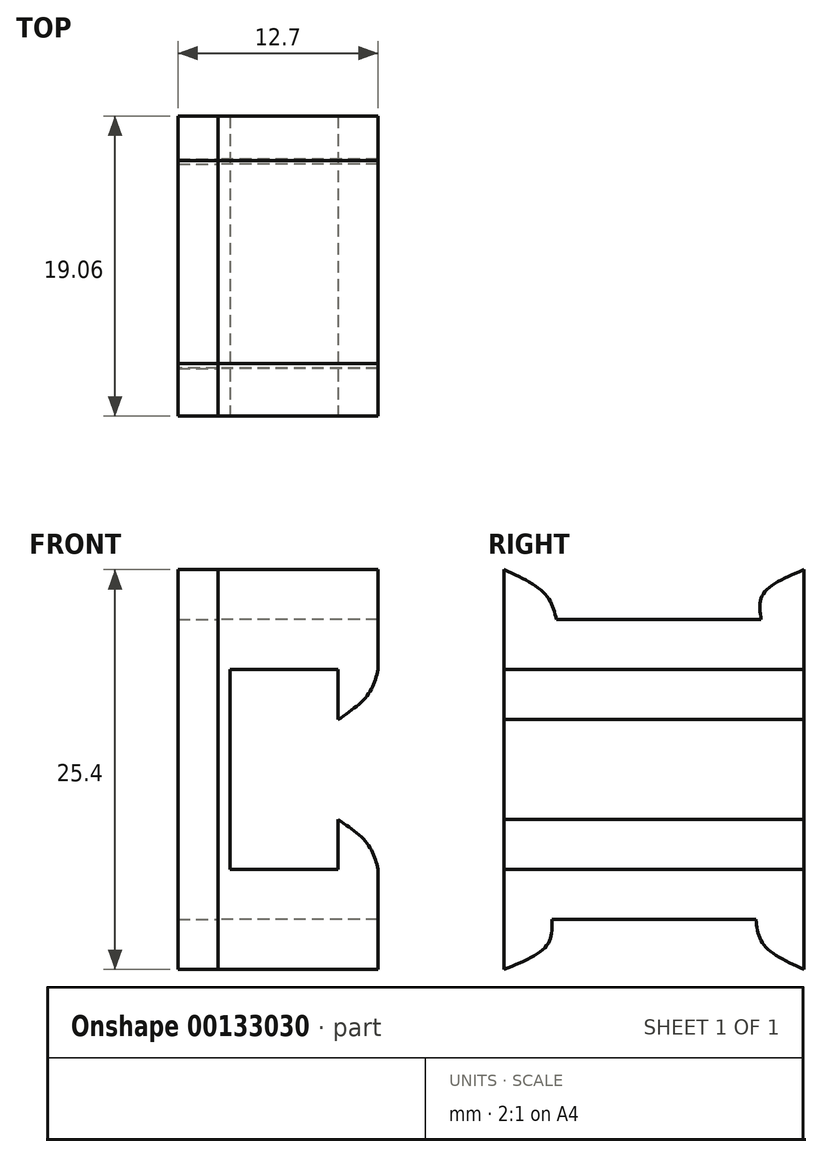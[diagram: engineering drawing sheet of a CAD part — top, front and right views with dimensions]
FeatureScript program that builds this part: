
annotation { "Feature Type Name" : "Feature", "Feature Type Description" : "" }
export const myFeature = defineFeature(function(context is Context, id is Id, definition is map)
    precondition{}
    {
        {
            var Q0;
            Q0=qCreatedBy(makeId("Right.planeOp"),FACE);
            var sketch = newSketch(context, id + "F0", { "sketchPlane" : qUnion([Q0])});
            skLineSegment(sketch, "E0.bottom", {"start": v(-9.53, 23.71) * mm, "end": v(9.52, 23.71) * mm});
            skLineSegment(sketch, "E0.top", {"start": v(-9.53, 42.76) * mm, "end": v(9.52, 42.76) * mm});
            skLineSegment(sketch, "E0.left", {"start": v(-9.53, 23.71) * mm, "end": v(-9.53, 42.76) * mm});
            skLineSegment(sketch, "E0.right", {"start": v(9.52, 23.71) * mm, "end": v(9.52, 42.76) * mm});
            skPoint(sketch, "E0.middle", {"position": v(0, 33.24) * mm});
            skLineSegment(sketch, "E1", {"start": v(9.52, 42.76) * mm, "end": v(9.52, 45.94) * mm});
            skLineSegment(sketch, "E2", {"start": v(-9.53, 42.76) * mm, "end": v(-9.53, 45.94) * mm});
            skLineSegment(sketch, "E3", {"start": v(-9.53, 23.71) * mm, "end": v(-9.53, 20.54) * mm});
            skLineSegment(sketch, "E4", {"start": v(9.52, 23.71) * mm, "end": v(9.52, 20.54) * mm});
            skPoint(sketch, "E5.1.internal.snap0", {"position": v(9.52, 22.13) * mm});
            skFitSpline(sketch, "E5", {"points": [v(9.53, 20.54) * mm, v(6.95, 22.13) * mm, v(6.47, 23.71) * mm], "startDerivative": vector(-5.44, 2.49) * mm, "endDerivative": vector(-0.42, 3.94) * mm});
            skFitSpline(sketch, "E6", {"points": [v(-9.52, 20.54) * mm, v(-6.77, 22.13) * mm, v(-6.5, 23.71) * mm], "startDerivative": vector(5.9, 2.4) * mm, "endDerivative": vector(-0.18, 4.04) * mm});
            skPoint(sketch, "E7.1.internal.snap0", {"position": v(-9.53, 44.35) * mm});
            skFitSpline(sketch, "E7", {"points": [v(-9.52, 45.94) * mm, v(-6.9, 44.35) * mm, v(-6.2, 42.76) * mm], "startDerivative": vector(5.47, -2.52) * mm, "endDerivative": vector(0.98, -3.9) * mm});
            skFitSpline(sketch, "E8", {"points": [v(9.53, 45.94) * mm, v(6.9, 44.35) * mm, v(6.8, 42.76) * mm], "startDerivative": vector(-5.76, -2.42) * mm, "endDerivative": vector(0.66, -4.01) * mm});
            skSolve(sketch);
        }
        {
            var Q0;
            {var subQ0=sQuery(id+"F0.wireOp",EDGE,"E0.left");Q0=makeQuery(id+"F0.imprint","IMPRINT",FACE,{"disambiguationData":[TD([[makeQuery(id+"F0.imprint","IMPRINT",EDGE,{"derivedFrom":subQ0}),-1.0]])]});}
            var Q1;
            {var subQ0=sQuery(id+"F0.wireOp",EDGE,"E2");Q1=makeQuery(id+"F0.imprint","IMPRINT",FACE,{"disambiguationData":[TD([[makeQuery(id+"F0.imprint","IMPRINT",EDGE,{"derivedFrom":subQ0}),-1.0]])]});}
            var Q2;
            {var subQ0=sQuery(id+"F0.wireOp",EDGE,"E1");Q2=makeQuery(id+"F0.imprint","IMPRINT",FACE,{"disambiguationData":[TD([[makeQuery(id+"F0.imprint","IMPRINT",EDGE,{"derivedFrom":subQ0}),1.0]])]});}
            var Q3;
            {var subQ0=sQuery(id+"F0.wireOp",EDGE,"E3");Q3=makeQuery(id+"F0.imprint","IMPRINT",FACE,{"disambiguationData":[TD([[makeQuery(id+"F0.imprint","IMPRINT",EDGE,{"derivedFrom":subQ0}),1.0]])]});}
            var Q4;
            {var subQ0=sQuery(id+"F0.wireOp",EDGE,"E4");Q4=makeQuery(id+"F0.imprint","IMPRINT",FACE,{"disambiguationData":[TD([[makeQuery(id+"F0.imprint","IMPRINT",EDGE,{"derivedFrom":subQ0}),-1.0]])]});}
            extrude(context, id + "F1", {"entities" : qUnion([Q0, Q1, Q2, Q3, Q4]), "endBound" : BoundingType.SYMMETRIC, "depth" : 10.16 * mm});
        }
        {
            var Q0;
            Q0=makeQuery(id+"F1.opExtrude","SWEPT_FACE",FACE,{"disambiguationData":[OSD([sQuery(id+"F0.wireOp",EDGE,"E0.left"),sQuery(id+"F0.wireOp",EDGE,"E2"),sQuery(id+"F0.wireOp",EDGE,"E3")])]});
            var sketch = newSketch(context, id + "F2", { "sketchPlane" : qUnion([Q0])});
            skPoint(sketch, "E9.endSnap0", {"position": v(0, 45.94) * mm});
            skLineSegment(sketch, "E10", {"start": v(-4.32, 39.59) * mm, "end": v(5.08, 39.59) * mm});
            skLineSegment(sketch, "E11", {"start": v(-4.32, 26.89) * mm, "end": v(5.08, 26.89) * mm});
            skLineSegment(sketch, "E12", {"start": v(-4.32, 39.59) * mm, "end": v(-4.32, 26.89) * mm});
            skSolve(sketch);
        }
        {
            var Q0;
            {var subQ0=sQuery(id+"F2.wireOp",EDGE,"E10");Q0=makeQuery(id+"F2.imprint","IMPRINT",FACE,{"disambiguationData":[TD([[makeQuery(id+"F2.imprint","IMPRINT",EDGE,{"derivedFrom":subQ0}),-1.0]])]});}
            extrude(context, id + "F3", {"entities" : qUnion([Q0]), "operationType" : NewBodyOperationType.REMOVE, "oppositeDirection" : true, "depth" : 36.4 * mm});
        }
        {
            var Q0;
            {var subQ0=sQuery(id+"F0.wireOp",EDGE,"E4");var subQ1=sQuery(id+"F0.wireOp",EDGE,"E1");var subQ2=sQuery(id+"F0.wireOp",EDGE,"E0.right");var subQ3=sQuery(id+"F0.wireOp",EDGE,"E3");var subQ4=sQuery(id+"F0.wireOp",EDGE,"E2");var subQ5=sQuery(id+"F0.wireOp",EDGE,"E0.left");var subQ6=sQuery(id+"F0.wireOp",EDGE,"E7");var subQ7=sQuery(id+"F0.wireOp",EDGE,"E0.top");var subQ8=sQuery(id+"F0.wireOp",EDGE,"E8");Q0=makeQuery(id+"F3.boolean.opBoolean","SPLIT",FACE,{"disambiguationData":[TD([makeQuery(id+"F1.opExtrude","SWEPT_FACE",FACE,{"disambiguationData":[OSD([subQ7])]})])],"derivedFrom":makeQuery(id+"F1.opExtrude","CAP_FACE",FACE,{"disambiguationData":[OSD([sQuery(id+"F0.wireOp",EDGE,"E0.bottom"),subQ7,subQ5,subQ2,subQ1,subQ4,subQ3,subQ0,sQuery(id+"F0.wireOp",EDGE,"E5"),sQuery(id+"F0.wireOp",EDGE,"E6"),subQ6,subQ8])],"isStart":false})});}
            var sketch = newSketch(context, id + "F4", { "sketchPlane" : qUnion([Q0])});
            skLineSegment(sketch, "E13", {"start": v(-9.53, 39.59) * mm, "end": v(-9.53, 36.41) * mm});
            skLineSegment(sketch, "E14", {"start": v(9.52, 39.59) * mm, "end": v(9.52, 36.41) * mm});
            skLineSegment(sketch, "E15", {"start": v(9.52, 36.41) * mm, "end": v(-9.53, 36.41) * mm});
            skLineSegment(sketch, "E16", {"start": v(-9.53, 39.59) * mm, "end": v(9.52, 39.59) * mm});
            skSolve(sketch);
        }
        {
            var Q0;
            {var subQ0=sQuery(id+"F0.wireOp",EDGE,"E5");var subQ1=sQuery(id+"F0.wireOp",EDGE,"E4");var subQ2=sQuery(id+"F0.wireOp",EDGE,"E1");var subQ3=sQuery(id+"F0.wireOp",EDGE,"E0.right");var subQ4=sQuery(id+"F0.wireOp",EDGE,"E3");var subQ5=sQuery(id+"F0.wireOp",EDGE,"E2");var subQ6=sQuery(id+"F0.wireOp",EDGE,"E0.left");var subQ7=sQuery(id+"F0.wireOp",EDGE,"E0.bottom");var subQ8=sQuery(id+"F0.wireOp",EDGE,"E6");Q0=makeQuery(id+"F3.boolean.opBoolean","SPLIT",FACE,{"disambiguationData":[TD([makeQuery(id+"F1.opExtrude","SWEPT_FACE",FACE,{"disambiguationData":[OSD([subQ7])]})])],"derivedFrom":makeQuery(id+"F1.opExtrude","CAP_FACE",FACE,{"disambiguationData":[OSD([subQ7,sQuery(id+"F0.wireOp",EDGE,"E0.top"),subQ6,subQ3,subQ2,subQ5,subQ4,subQ1,subQ0,subQ8,sQuery(id+"F0.wireOp",EDGE,"E7"),sQuery(id+"F0.wireOp",EDGE,"E8")])],"isStart":false})});}
            var sketch = newSketch(context, id + "F5", { "sketchPlane" : qUnion([Q0])});
            skLineSegment(sketch, "E17", {"start": v(-9.53, 26.89) * mm, "end": v(-9.53, 30.06) * mm});
            skLineSegment(sketch, "E18", {"start": v(-9.53, 30.06) * mm, "end": v(9.52, 30.06) * mm});
            skLineSegment(sketch, "E19", {"start": v(9.52, 30.06) * mm, "end": v(9.52, 26.89) * mm});
            skSolve(sketch);
        }
        {
            var Q0;
            Q0=makeQuery(id+"F5.imprint","IMPRINT",FACE,{"disambiguationData":[TD([[makeQuery(id+"F5.imprint","IMPRINT",EDGE,{"derivedFrom":sQuery(id+"F5.wireOp",EDGE,"E17")}),-1.0]])]});
            var Q1;
            Q1=makeQuery(id+"F4.imprint","IMPRINT",FACE,{"disambiguationData":[TD([[makeQuery(id+"F4.imprint","IMPRINT",EDGE,{"derivedFrom":sQuery(id+"F4.wireOp",EDGE,"E13")}),1.0]])]});
            extrude(context, id + "F6", {"entities" : qUnion([Q0, Q1]), "operationType" : NewBodyOperationType.ADD, "oppositeDirection" : true, "depth" : 2.54 * mm});
        }
        {
            var Q0;
            Q0=makeQuery(id+"F6.boolean.opBoolean","MERGE",FACE,{"derivedFrom":[makeQuery(id+"F1.opExtrude","SWEPT_FACE",FACE,{"disambiguationData":[OSD([sQuery(id+"F0.wireOp",EDGE,"E0.left"),sQuery(id+"F0.wireOp",EDGE,"E2"),sQuery(id+"F0.wireOp",EDGE,"E3")])]}),makeQuery(id+"F6.opExtrude","SWEPT_FACE",FACE,{"disambiguationData":[OSD([sQuery(id+"F4.wireOp",EDGE,"E13")])]}),makeQuery(id+"F6.opExtrude","SWEPT_FACE",FACE,{"disambiguationData":[OSD([sQuery(id+"F5.wireOp",EDGE,"E17")])]})]});
            var sketch = newSketch(context, id + "F7", { "sketchPlane" : qUnion([Q0])});
            skPoint(sketch, "E20.endSnap0", {"position": v(2.54, 38) * mm});
            skLineSegment(sketch, "E21", {"start": v(2.54, 26.89) * mm, "end": v(5.08, 26.89) * mm});
            skLineSegment(sketch, "E22", {"start": v(2.54, 39.59) * mm, "end": v(5.08, 39.59) * mm});
            skFitSpline(sketch, "E23", {"points": [v(5.08, 39.59) * mm, v(4.45, 38) * mm, v(2.54, 36.41) * mm], "startDerivative": vector(-0.93, -3.63) * mm, "endDerivative": vector(-4.06, -2.74) * mm});
            skFitSpline(sketch, "E24", {"points": [v(5.08, 26.89) * mm, v(4.45, 28.48) * mm, v(2.54, 30.06) * mm], "startDerivative": vector(-0.93, 3.63) * mm, "endDerivative": vector(-4.06, 2.74) * mm});
            skSolve(sketch);
        }
        {
            var Q0;
            {var subQ0=sQuery(id+"F7.wireOp",EDGE,"E23");Q0=makeQuery(id+"F7.imprint","IMPRINT",FACE,{"disambiguationData":[TD([[makeQuery(id+"F7.imprint","IMPRINT",EDGE,{"derivedFrom":subQ0}),1.0]])]});}
            var Q1;
            {var subQ0=sQuery(id+"F7.wireOp",EDGE,"E24");Q1=makeQuery(id+"F7.imprint","IMPRINT",FACE,{"disambiguationData":[TD([[makeQuery(id+"F7.imprint","IMPRINT",EDGE,{"derivedFrom":subQ0}),-1.0]])]});}
            extrude(context, id + "F8", {"entities" : qUnion([Q0, Q1]), "operationType" : NewBodyOperationType.REMOVE, "oppositeDirection" : true, "depth" : 25.4 * mm});
        }
        {
            var Q0;
            Q0=makeQuery(id+"F1.opExtrude","CAP_FACE",FACE,{"disambiguationData":[OSD([sQuery(id+"F0.wireOp",EDGE,"E0.bottom"),sQuery(id+"F0.wireOp",EDGE,"E0.top"),sQuery(id+"F0.wireOp",EDGE,"E0.left"),sQuery(id+"F0.wireOp",EDGE,"E0.right"),sQuery(id+"F0.wireOp",EDGE,"E1"),sQuery(id+"F0.wireOp",EDGE,"E2"),sQuery(id+"F0.wireOp",EDGE,"E3"),sQuery(id+"F0.wireOp",EDGE,"E4"),sQuery(id+"F0.wireOp",EDGE,"E5"),sQuery(id+"F0.wireOp",EDGE,"E6"),sQuery(id+"F0.wireOp",EDGE,"E7"),sQuery(id+"F0.wireOp",EDGE,"E8")])],"isStart":true});
            var sketch = newSketch(context, id + "F9", { "sketchPlane" : qUnion([Q0])});
            skSolve(sketch);
        }
        {
            var Q0;
            Q0=makeQuery(id+"F9.imprint","IMPRINT",FACE,{"disambiguationData":[TD([[makeQuery(id+"F9.imprint","IMPRINT",EDGE,{"derivedFrom":makeQuery(id+"F1.opExtrude","CAP_EDGE",EDGE,{"disambiguationData":[OSD([sQuery(id+"F0.wireOp",EDGE,"E0.bottom")])],"isStart":true})}),-1.0]])]});
            extrude(context, id + "F10", {"entities" : qUnion([Q0]), "depth" : 2.54 * mm});
        }
    });
